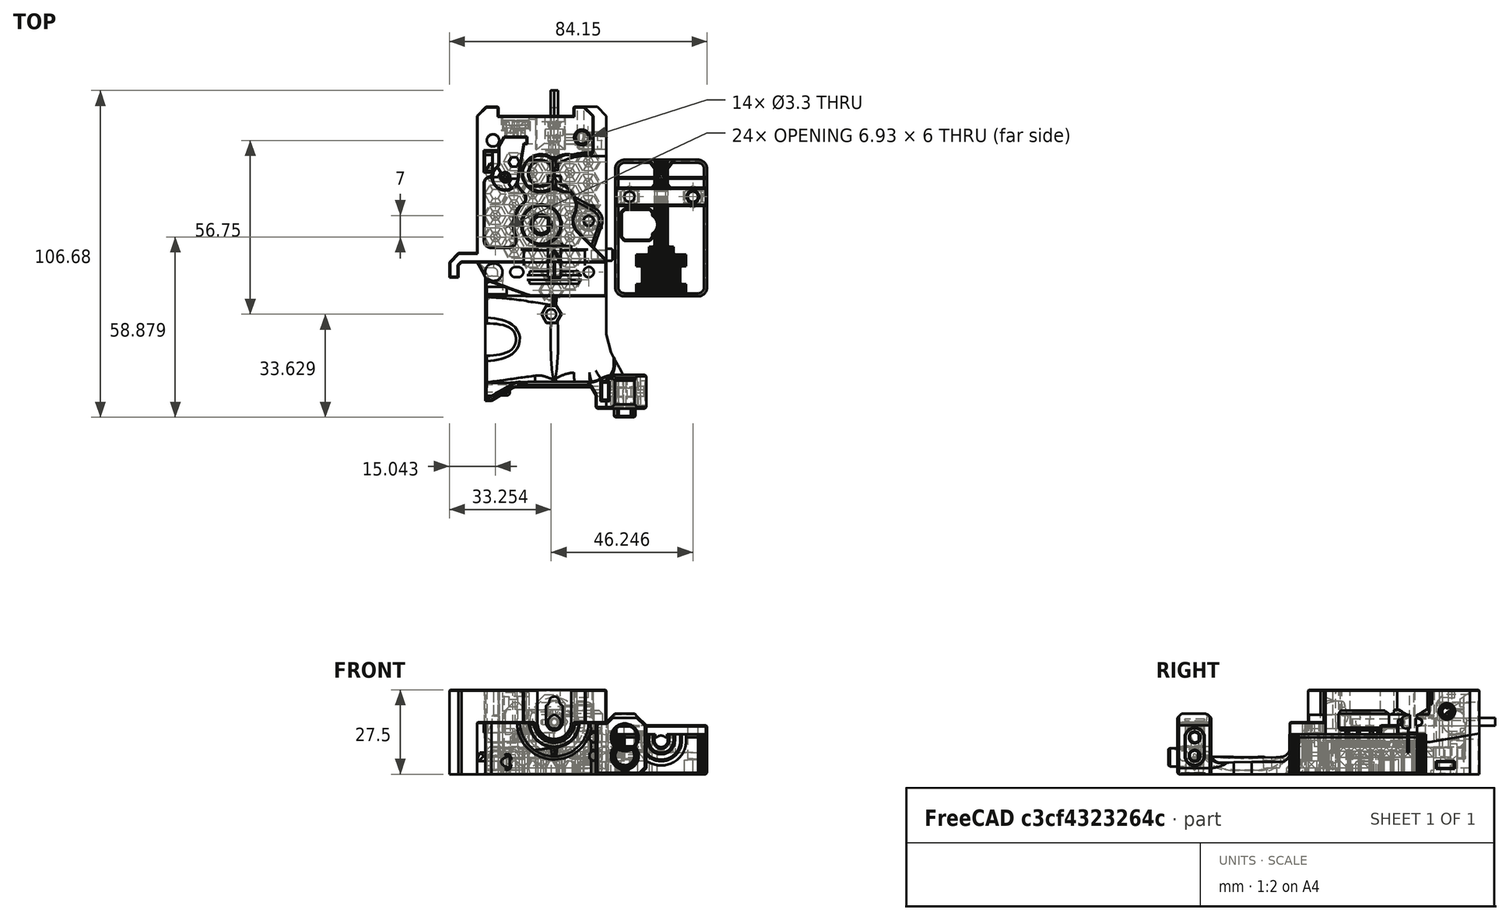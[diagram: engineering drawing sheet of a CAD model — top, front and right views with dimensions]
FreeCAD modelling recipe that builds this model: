
FCSTD DOCUMENT  (FreeCAD 0.18R14555 (Git shallow))
Label: PTFE-BMG-v2
License: All rights reserved
LicenseURL: http://en.wikipedia.org/wiki/All_rights_reserved
objects: Part::Cut×34, Part::Feature×32, Part::Box×29, Part::Cylinder×24, Part::MultiFuse×20, Part::Chamfer×8, Part::MultiCommon×4, App::DocumentObjectGroup×3, Sketcher::SketchObject×1, PartDesign::Pad×1, PartDesign::Body×1
note: 155 computed .brp shape members not serialized (recipe doc carries the construction recipe); baked Part::Feature solids carry a one-line shape summary decoded from their .brp

FEATURE [Part::Feature] Part__Feature001  label="ptfe-insert"
  Placement = pos=(4.72,10,0) rot=(0,0,1;0rad)
  shape: bbox 6.822 x 10.5 x 11.73 mm, 34 faces (baked)
FEATURE [Part::Feature] Part__Feature002  label="ptfe-path"
  Placement = pos=(4.72,17,0) rot=(0,0,1;0rad)
  shape: bbox 4.25 x 24 x 4.45 mm, 6 faces (baked)
FEATURE [Part::Feature] Part__Feature003  label="filament-path"
  Placement = pos=(4.72,30,0) rot=(0,0,1;0rad)
  shape: bbox 2.35 x 16 x 2.55 mm, 14 faces (baked)
FEATURE [Part::Feature] PTFE_CUTTER_1_0_1_001001_solid  label="PTFE_CUTTER"
  Placement = pos=(37.03,-6.87,0) rot=(0,0,1;0rad)
  shape: bbox 30 x 35 x 16 mm, 2095 faces (baked)
FEATURE [Part::Box] Box  label="Cube"
  AttacherType = Attacher::AttachEngine3D
  Height = 17
  Length = 33
  Placement = pos=(20,6,0) rot=(0,0,1;0rad)
  Width = 1
FEATURE [Part::Feature] PTFE_CUTTER_1_0_1_001001_solid001  label="PTFE_CUTTER001"
  Placement = pos=(37.03,-6.87,0) rot=(0,0,1;0rad)
  shape: bbox 30 x 35 x 16 mm, 2095 faces (baked)
FEATURE [Part::MultiCommon] Common
  Placement = pos=(0,18.58,0) rot=(0,0,1;0rad)
  Shapes = -> [Box,PTFE_CUTTER_1_0_1_001001_solid001]
FEATURE [Part::Box] Box001  label="Cube001"
  AttacherType = Attacher::AttachEngine3D
  Height = 18
  Length = 32
  Placement = pos=(20,16.32,0) rot=(0,0,1;0rad)
  Width = 6
FEATURE [Part::Box] Box002  label="Cube002"
  AttacherType = Attacher::AttachEngine3D
  Height = 18
  Length = 32
  Placement = pos=(20,16,0) rot=(0,0,1;0rad)
  Width = 15
FEATURE [Part::Feature] PTFE_CUTTER_1_0_1_001001_solid002  label="PTFE_CUTTER002"
  Placement = pos=(37.03,-6.87,0) rot=(0,0,1;0rad)
  shape: bbox 30 x 35 x 16 mm, 2095 faces (baked)
FEATURE [Part::MultiCommon] Common001
  Placement = pos=(0,9.58,0) rot=(0,0,1;0rad)
  Shapes = -> [Box002,PTFE_CUTTER_1_0_1_001001_solid002]
FEATURE [Part::Box] Box003  label="Cube003"
  AttacherType = Attacher::AttachEngine3D
  Height = 18
  Length = 32
  Placement = pos=(20,7,0) rot=(0,0,1;0rad)
  Width = 11
FEATURE [Part::Feature] PTFE_CUTTER_1_0_1_001001_solid003  label="PTFE_CUTTER003"
  Placement = pos=(37.03,-6.87,0) rot=(0,0,1;0rad)
  shape: bbox 30 x 35 x 16 mm, 2095 faces (baked)
FEATURE [Part::MultiCommon] Common002
  Placement = pos=(0,6.58,0) rot=(0,0,1;0rad)
  Shapes = -> [Box003,PTFE_CUTTER_1_0_1_001001_solid003]
FEATURE [Part::Cut] Cut
  Base = -> PTFE_CUTTER_1_0_1_001001_solid
  Tool = -> Box001
FEATURE [Part::MultiFuse] Fusion
  Shapes = -> [Cut,Common002,Common001,Common]
FEATURE [Part::Box] Box004  label="Cube004"
  AttacherType = Attacher::AttachEngine3D
  Height = 10
  Length = 10
  Placement = pos=(23,7,6) rot=(0,0,1;0rad)
  Width = 17.7
FEATURE [Part::Box] Box005  label="Cube005"
  AttacherType = Attacher::AttachEngine3D
  Height = 10
  Length = 10
  Placement = pos=(23,25.5,6) rot=(0,0,1;0rad)
  Width = 3.7
FEATURE [Part::MultiFuse] Fusion001
  Shapes = -> [Box005,Box004,Fusion]
FEATURE [Part::Box] Box006  label="Cube006"
  AttacherType = Attacher::AttachEngine3D
  Height = 5
  Length = 1
  Placement = pos=(49.88,-10,1) rot=(0,0,1;0rad)
  Width = 37.5
FEATURE [Part::MultiFuse] Fusion002
  Shapes = -> [Box006,Fusion001]
FEATURE [Part::Box] Box007  label="Cube007"
  AttacherType = Attacher::AttachEngine3D
  Height = 21
  Length = 32
  Placement = pos=(20,13,0) rot=(0,0,1;0rad)
  Width = 2
FEATURE [Part::Feature] Fusion002001  label="Fusion003"
  shape: bbox 30 x 44.58 x 16 mm, 1730 faces (baked)
FEATURE [Part::MultiCommon] Common003
  Placement = pos=(0,-7,0) rot=(0,0,1;0rad)
  Shapes = -> [Box007,Fusion002001]
FEATURE [Part::MultiFuse] Fusion002002
  Shapes = -> [Common003,Fusion002]
FEATURE [Part::Cylinder] Cylinder005  label="ptfe-cut002"
  Angle = 360
  AttacherType = Attacher::AttachEngine3D
  Height = 22
  Placement = pos=(31.19,9.89,0) rot=(0,0,1;0rad)
  Radius = 3.4
FEATURE [Part::Box] Box010  label="Cube010"
  AttacherType = Attacher::AttachEngine3D
  Height = 10
  Length = 32
  Placement = pos=(20,-15,13) rot=(0,0,1;0rad)
  Width = 47
FEATURE [Part::Box] Box011  label="Cube011"
  AttacherType = Attacher::AttachEngine3D
  Height = 24
  Length = 10
  Placement = pos=(23,5,0) rot=(0,0,1;0rad)
  Width = 9.77
FEATURE [Part::Chamfer] Chamfer
  Base = -> Box011
  Edges = 4 edges r=1: [Edge1,Edge3,Edge5,Edge7]
FEATURE [Part::Cylinder] Cylinder006  label="Cylinder"
  Angle = 360
  AttacherType = Attacher::AttachEngine3D
  Height = 30
  Placement = pos=(25.52,19,0) rot=(0,0,1;0rad)
  Radius = 1.65
FEATURE [Part::Cylinder] Cylinder007  label="Cylinder001"
  Angle = 360
  AttacherType = Attacher::AttachEngine3D
  Height = 30
  Placement = pos=(46.23,19,0) rot=(0,0,1;0rad)
  Radius = 1.65
FEATURE [Part::Box] Box012  label="Cube012"
  AttacherType = Attacher::AttachEngine3D
  Height = 3
  Length = 30
  Placement = pos=(20.88,17,13) rot=(0,0,1;0rad)
  Width = 6
FEATURE [Part::Box] Box013  label="Cube013"
  AttacherType = Attacher::AttachEngine3D
  Height = 4
  Length = 3.8
  Placement = pos=(33.98,16,12) rot=(0,0,1;0rad)
  Width = 8
FEATURE [Part::Cylinder] Cylinder008  label="ptfe-tube-pref002"
  Angle = 360
  AttacherType = Attacher::AttachEngine3D
  Height = 32
  Placement = pos=(35.85,27,10.6) rot=(1,0,0;1.5708rad)
  Radius = 2
FEATURE [Part::Cut] Cut001008
  Base = -> Box013
  Placement = pos=(0,1,0) rot=(0,0,1;0rad)
  Tool = -> Cylinder008
FEATURE [Part::Cylinder] Cylinder009  label="Cylinder002"
  Angle = 360
  AttacherType = Attacher::AttachEngine3D
  Height = 30
  Placement = pos=(25.52,20,0) rot=(0,0,1;0rad)
  Radius = 1.65
FEATURE [Part::Cylinder] Cylinder010  label="Cylinder003"
  Angle = 360
  AttacherType = Attacher::AttachEngine3D
  Height = 30
  Placement = pos=(46.23,20,0) rot=(0,0,1;0rad)
  Radius = 1.65
FEATURE [Part::MultiFuse] Fusion002005
  Shapes = -> [Cylinder009,Cylinder010]
FEATURE [Part::Feature] Cut001012003001  label="Cut001012004"
  Placement = pos=(25.52,19,0) rot=(0,0,1;0rad)
  shape: bbox 5.543 x 6.4 x 5 mm, 28 faces (baked)
FEATURE [Part::Feature] Cut001012003002  label="Cut001012005"
  Placement = pos=(46.23,19,0) rot=(0,0,1;0rad)
  shape: bbox 5.543 x 6.4 x 5 mm, 28 faces (baked)
FEATURE [Part::Feature] Body001005  label="Body001"
  Placement = pos=(35.88,25.2,0) rot=(0,0,1;0rad)
  shape: bbox 6.881 x 4.788 x 40 mm, 8 faces (baked)
FEATURE [Part::Feature] Body001006  label="Body002"
  Placement = pos=(35.88,26.02,0) rot=(0,0,1;3.14159rad)
  shape: bbox 12.97 x 8.755 x 40 mm, 8 faces (baked)
FEATURE [Part::Feature] Body001007  label="Body003"
  Placement = pos=(35.88,25.2,10.5) rot=(0,0,1;0rad)
  shape: bbox 12.18 x 7.934 x 34 mm, 5 faces (baked)
FEATURE [Part::MultiFuse] Fusion002008
  Placement = pos=(0,0,7) rot=(0,0,1;0rad)
  Shapes = -> [Body001005,Body001006]
FEATURE [Part::Cut] Cut001012003003
  Base = -> Fusion002002
  Tool = -> Fusion002008
FEATURE [Part::Cut] Cut001012003004
  Base = -> Cut001012003003
  Tool = -> Body001007
FEATURE [Part::Cut] Cut001012003005
  Base = -> Cut001012003004
  Tool = -> Cylinder005
FEATURE [Part::Cut] Cut001012003006
  Base = -> Cut001012003005
  Tool = -> Chamfer
FEATURE [Part::Feature] Part__Feature008  label="filament-path001"
  Placement = pos=(4.72,40,0) rot=(0,0,1;0rad)
  shape: bbox 2.35 x 16 x 2.55 mm, 14 faces (baked)
FEATURE [Part::Cut] Cut001012003011002008002
  Base = -> Cut001012003006
  Tool = -> Cylinder006
FEATURE [Part::Cut] Cut001012003011002008003
  Base = -> Cut001012003011002008002
  Tool = -> Cylinder007
FEATURE [Part::Cut] Cut001012003011002008004
  Base = -> Cut001012003011002008003
  Tool = -> Cut001012003002
FEATURE [Part::Cut] Cut001012003011002008005
  Base = -> Cut001012003011002008004
  Tool = -> Cut001012003001
FEATURE [Part::Cut] Cut001012003011002008006  label="cutter-base"
  Base = -> Cut001012003011002008005
  Tool = -> Box010
FEATURE [Part::Feature] Cut001012003011002008006002  label="cutter-base001"
  shape: bbox 30 x 44.58 x 13 mm, 1519 faces (baked)
FEATURE [Part::Chamfer] Chamfer002002
  Base = -> Cut001012003011002008006002
  Edges = 37 edges r=0.4: [Edge442,Edge443,Edge444,Edge445,Edge446,Edge447,Edge448,Edge449,Edge450,Edge451,Edge452,Edge453,Edge454,Edge455,Edge456,Edge457,Edge458,Edge459,Edge460,Edge461,Edge462,Edge463,Edge464,Edge465,Edge546,Edge549,Edge550,Edge551,Edge552,Edge553,Edge592,Edge593,Edge594,Edge595,Edge596,Edge597,Edge1307]
FEATURE [Part::Chamfer] Chamfer002003  label="cutter-base-rf"
  Base = -> Chamfer002002
  Edges = 8 edges r=1: [Edge389,Edge392,Edge417,Edge421,Edge506,Edge508,Edge530,Edge534]
FEATURE [Part::Box] Box019  label="Cube019"
  AttacherType = Attacher::AttachEngine3D
  Height = 10
  Length = 10
  Placement = pos=(30,23,8) rot=(0,0,1;0rad)
  Width = 10
FEATURE [Part::Cut] Cut001012003011002008006003
  Base = -> Cut001008
  Tool = -> Box019
FEATURE [Part::Cut] Cut001012003011002008006004
  Base = -> Box012
  Tool = -> Fusion002005
FEATURE [Part::MultiFuse] Fusion002009
  Shapes = -> [Cut001012003011002008006004,Cut001012003011002008006003]
FEATURE [Part::Chamfer] Chamfer002004  label="cutter-cap"
  Base = -> Fusion002009
  Edges = 13 edges r=0.4: [Edge1,Edge2,Edge3,Edge7,Edge8,Edge17,Edge18,Edge31,Edge32,Edge33,Edge34,Edge35,Edge41]
  Placement = pos=(0,-1,0) rot=(0,0,1;0rad)
FEATURE [Part::Box] Box028  label="Cube028"
  AttacherType = Attacher::AttachEngine3D
  Height = 3.35
  Length = 8
  Placement = pos=(8.5,8.5,10.7) rot=(0,0,1;0rad)
  Width = 1
FEATURE [Part::Box] Box029  label="hingle-support-p3"
  AttacherType = Attacher::AttachEngine3D
  Height = 3.35
  Length = 7
  Placement = pos=(8.5,12.8,10.7) rot=(0,0,1;0rad)
  Width = 1
FEATURE [Part::Box] Box030  label="hingle-support-p4"
  AttacherType = Attacher::AttachEngine3D
  Height = 3.35
  Length = 5
  Placement = pos=(9,15.1,10.7) rot=(0,0,1;0rad)
  Width = 1
FEATURE [Part::Box] Box031  label="Cube031"
  AttacherType = Attacher::AttachEngine3D
  Height = 3.35
  Length = 3
  Placement = pos=(11.7,4.8,10.7) rot=(0,0,1;0rad)
  Width = 1
FEATURE [Part::Chamfer] Chamfer002005  label="hingle-support-p2"
  Base = -> Box028
  Edges = 1 edges r=0.5: [Edge1]
FEATURE [Part::Chamfer] Chamfer002006  label="hingle-support-p1"
  Base = -> Box031
  Edges = 1 edges r=0.5: [Edge1]
FEATURE [Part::Cylinder] Cylinder015  label="Cylinder008"
  Angle = 360
  AttacherType = Attacher::AttachEngine3D
  Height = 10
  Placement = pos=(24,-43,6) rot=(1,0,0;1.5708rad)
  Radius = 3.5
FEATURE [Part::Cylinder] Cylinder016  label="Cylinder009"
  Angle = 360
  AttacherType = Attacher::AttachEngine3D
  Height = 10
  Placement = pos=(24,-43,11.5) rot=(1,0,0;1.5708rad)
  Radius = 3.6
FEATURE [Part::Cut] Cut001012003011002008006006009003002
  Base = -> Cylinder015
  Tool = -> Cylinder016
FEATURE [Part::Cylinder] Cylinder017  label="Cylinder010"
  Angle = 360
  AttacherType = Attacher::AttachEngine3D
  Height = 10
  Placement = pos=(19,-48,6) rot=(0,1,0;1.5708rad)
  Radius = 1.65
FEATURE [Part::Cylinder] Cylinder018  label="Cylinder011"
  Angle = 360
  AttacherType = Attacher::AttachEngine3D
  Height = 10
  Placement = pos=(19,-46.6,6) rot=(0,1,0;1.5708rad)
  Radius = 0.5
FEATURE [Part::Cut] Cut001012003011002008006006009003003
  Base = -> Cut001012003011002008006006009003002
  Tool = -> Cylinder017
FEATURE [Part::Cut] Cut001012003011002008006006009003004
  Base = -> Cut001012003011002008006006009003003
  Tool = -> Cylinder018
FEATURE [Part::Chamfer] Chamfer002007  label="brope-spacer"
  Base = -> Cut001012003011002008006006009003004
  Edges = 8 edges r=0.4: [Edge1,Edge2,Edge8,Edge12,Edge13,Edge14,Edge15,Edge16]
FEATURE [Part::Box] Box034  label="probe-support002"
  AttacherType = Attacher::AttachEngine3D
  Height = 0.2
  Length = 9
  Placement = pos=(22,-49,0) rot=(0,0,1;0rad)
  Width = 8
FEATURE [Part::Box] Box035  label="probe-support-mid"
  AttacherType = Attacher::AttachEngine3D
  Height = 0.2
  Length = 9
  Placement = pos=(19.5,-49,8.9) rot=(0,0,1;0rad)
  Width = 8
FEATURE [App::DocumentObjectGroup] Group  label="Cutter-guide"
  Group = -> [Cut001012003011002008006,Chamfer002003,Chamfer002004]
FEATURE [App::DocumentObjectGroup] Group002  label="Other"
  Group = -> [Chamfer002007]
FEATURE [Part::Feature] Cut001012003011002008006006009003008001  label="hex-cut-origin-p003"
  shape: bbox 6.928 x 6 x 4 mm, 14 faces (baked)
FEATURE [Part::Feature] Cut001012003011002008006006009003007001  label="hex-cut-origin-p004"
  shape: bbox 37.24 x 34 x 4 mm, 336 faces, 24 solids (baked)
FEATURE [Part::Feature] Cut001012003011002008006006009003008002  label="hex-cut-origin-p005"
  Placement = pos=(0,0,2.5) rot=(0,0,1;0rad)
  shape: bbox 6.928 x 6 x 4 mm, 14 faces (baked)
FEATURE [Part::Feature] Cut001012003011002008006006009003008003  label="hex-cut-origin-p006"
  Placement = pos=(0,0,2.5) rot=(0,0,1;0rad)
  shape: bbox 37.24 x 34 x 4 mm, 336 faces, 24 solids (baked)
FEATURE [Part::Feature] Cut001012003011002008006006009003008004  label="hex-cut-origin-p007"
  Placement = pos=(0,0,5) rot=(0,0,1;0rad)
  shape: bbox 37.24 x 34 x 4 mm, 336 faces, 24 solids (baked)
FEATURE [Part::MultiFuse] Fusion002010004002002006  label="full-back-hex-cut"
  Shapes = -> [Cut001012003011002008006006009003008001,Cut001012003011002008006006009003008003,Cut001012003011002008006006009003007001,Cut001012003011002008006006009003008002,Cut001012003011002008006006009003008004]
FEATURE [Part::Cylinder] Cylinder  label="scew-hole"
  Angle = 360
  AttacherType = Attacher::AttachEngine3D
  Height = 11
  Placement = pos=(12.25,11.13,0) rot=(0,0,1;0rad)
  Radius = 1.6
FEATURE [Part::Cylinder] Cylinder020  label="Cylinder013"
  Angle = 360
  AttacherType = Attacher::AttachEngine3D
  Height = 3.4
  Radius = 3
FEATURE [Part::Box] Box038  label="Cube032"
  AttacherType = Attacher::AttachEngine3D
  Height = 0.2
  Length = 5
  Placement = pos=(1.6,-5,3.2) rot=(0,0,1;0rad)
  Width = 10
FEATURE [Part::Box] Box039  label="Cube033"
  AttacherType = Attacher::AttachEngine3D
  Height = 0.2
  Length = 5
  Placement = pos=(-6.6,-5,3.2) rot=(0,0,1;0rad)
  Width = 10
FEATURE [Part::Box] Box040  label="Cube034"
  AttacherType = Attacher::AttachEngine3D
  Height = 0.4
  Length = 10
  Placement = pos=(-5,-6.6,3) rot=(0,0,1;0rad)
  Width = 5
FEATURE [Part::Box] Box041  label="Cube035"
  AttacherType = Attacher::AttachEngine3D
  Height = 0.4
  Length = 10
  Placement = pos=(-5,1.6,3) rot=(0,0,1;0rad)
  Width = 5
FEATURE [Part::MultiFuse] Fusion002010004002002006003002002002
  Shapes = -> [Box039,Box041,Box038,Box040]
FEATURE [Part::Cut] Cut001012003011002008006006009003008009
  Base = -> Cylinder020
  Placement = pos=(12.25,11.13,0) rot=(0,0,1;0rad)
  Tool = -> Fusion002010004002002006003002002002
FEATURE [Part::Cylinder] Cylinder022  label="screw-base-fill"
  Angle = 360
  AttacherType = Attacher::AttachEngine3D
  Height = 7
  Placement = pos=(12.25,11.13,0) rot=(0,0,1;0rad)
  Radius = 5.3
FEATURE [Part::MultiFuse] Fusion002010004002002006003002002004  label="back-screw"
  Shapes = -> [Cut001012003011002008006006009003008009,Cylinder]
FEATURE [Part::Feature] Fusion002010004002002006003002002004001  label="back-screw001"
  shape: bbox 6 x 6 x 11 mm, 16 faces (baked)
FEATURE [Part::Box] Box043  label="Cube037"
  AttacherType = Attacher::AttachEngine3D
  Height = 11.5
  Length = 2.2
  Placement = pos=(0,38.98,0) rot=(0,0,1;0rad)
  Width = 9.15
FEATURE [Part::Feature] Part__Feature025009  label="Original-v2"
  Placement = pos=(-24,-68,-52.6717) rot=(0,0,1;0rad)
  shape: bbox 64.27 x 98.52 x 42.65 mm, 988 faces (baked)
FEATURE [Part::Feature] Part__Feature025009001  label="Original-v003"
  Placement = pos=(-24,-68,-52.6717) rot=(0,0,1;0rad)
  shape: bbox 64.27 x 98.52 x 42.65 mm, 988 faces (baked)
FEATURE [Part::MultiFuse] Fusion002010004002002006003002002004003  label="full-custom-support"
  Shapes = -> [Box034,Box035,Chamfer002006,Chamfer002005,Box029,Box030]
FEATURE [App::DocumentObjectGroup] Group001  label="Support"
  Group = -> [Fusion002010004002002006003002002004003]
FEATURE [Part::Feature] Fusion002010004002002006002001  label="full-filament-path001"
  shape: bbox 2.35 x 26 x 2.55 mm, 5 faces (baked)
FEATURE [Part::MultiFuse] Fusion002010004002002006002  label="full-filament-path"
  Shapes = -> [Part__Feature008,Part__Feature003]
FEATURE [Part::Feature] Part__Feature002001  label="ptfp1"
  Placement = pos=(4.72,17,0) rot=(0,0,1;0rad)
  shape: bbox 4.25 x 24 x 4.45 mm, 6 faces (baked)
FEATURE [Part::MultiFuse] Fusion002010004002002006003002002004003002  label="full-ptfe-path"
  Shapes = -> [Part__Feature002,Part__Feature001]
FEATURE [Part::Feature] Part__Feature025009002  label="ptfp002"
  Placement = pos=(4.72,8,0) rot=(0,0,1;0rad)
  shape: bbox 4.25 x 24 x 4.45 mm, 6 faces (baked)
FEATURE [Part::MultiFuse] Fusion002010004002002006003002002004003003  label="long-ptfe-path"
  Shapes = -> [Part__Feature025009002,Part__Feature002001]
FEATURE [Part::Feature] Fusion002010004002002006003002002004003003001  label="long-ptfe-path001"
  shape: bbox 4.25 x 33 x 4.45 mm, 6 faces (baked)
FEATURE [Part::Cut] Cut001012003011002008006006009003008010
  Base = -> Part__Feature025009001
  Tool = -> Fusion002010004002002006003002002004003003001
FEATURE [Part::Cut] Cut001012003011002008006006009003008011
  Base = -> Cut001012003011002008006006009003008010
  Tool = -> Fusion002010004002002006002001
FEATURE [Part::Cylinder] Cylinder023  label="bolt-fill"
  Angle = 360
  AttacherType = Attacher::AttachEngine3D
  Height = 10
  Placement = pos=(1,33.38,7) rot=(-1,0,0;1.5708rad)
  Radius = 3
FEATURE [Part::Cylinder] Cylinder024  label="top-m3"
  Angle = 360
  AttacherType = Attacher::AttachEngine3D
  Height = 10
  Placement = pos=(1,33.38,7) rot=(-1,0,0;1.5708rad)
  Radius = 1.65
FEATURE [Part::Cylinder] Cylinder025  label="m3-printable-cut"
  Angle = 360
  AttacherType = Attacher::AttachEngine3D
  Height = 10
  Placement = pos=(1,33.38,8.5) rot=(-1,0,0;1.5708rad)
  Radius = 0.5
FEATURE [Part::Box] Box044  label="m3-square-nut"
  AttacherType = Attacher::AttachEngine3D
  Height = 10
  Length = 5.8
  Placement = pos=(-1.9,39,0) rot=(0,0,1;0rad)
  Width = 2.2
FEATURE [Part::Cylinder] Cylinder026  label="Cylinder014"
  Angle = 360
  AttacherType = Attacher::AttachEngine3D
  Height = 9.2
  Placement = pos=(4.53,37.9,20.5) rot=(0,1,0;1.5708rad)
  Radius = 3
FEATURE [Part::Cylinder] Cylinder027  label="m3"
  Angle = 360
  AttacherType = Attacher::AttachEngine3D
  Height = 9.2
  Placement = pos=(4.53,37.9,20.5) rot=(0,1,0;1.5708rad)
  Radius = 1.65
FEATURE [Part::Cylinder] Cylinder028  label="m004"
  Angle = 360
  AttacherType = Attacher::AttachEngine3D
  Height = 9.2
  Placement = pos=(4.53,37.9,22) rot=(0,1,0;1.5708rad)
  Radius = 0.5
FEATURE [Part::Box] Box045  label="Cube038"
  AttacherType = Attacher::AttachEngine3D
  Height = 6
  Length = 2.2
  Placement = pos=(8.53,34.9,17.6) rot=(0,0,1;0rad)
  Width = 19
FEATURE [Part::Cylinder] Cylinder029  label="Cylinder015"
  Angle = 360
  AttacherType = Attacher::AttachEngine3D
  Height = 14
  Placement = pos=(24,-51,15.8) rot=(-1,0,0;1.5708rad)
  Radius = 0.7
FEATURE [Part::Cylinder] Cylinder030  label="Cylinder016"
  Angle = 360
  AttacherType = Attacher::AttachEngine3D
  Height = 23
  Placement = pos=(35,-44.5,7.5) rot=(0,-1,0;1.5708rad)
  Radius = 0.5
FEATURE [Part::Cylinder] Cylinder031  label="Cylinder017"
  Angle = 360
  AttacherType = Attacher::AttachEngine3D
  Height = 23
  Placement = pos=(35,-44.5,13.5) rot=(0,-1,0;1.5708rad)
  Radius = 0.5
FEATURE [Part::Box] Box046  label="Cube039"
  AttacherType = Attacher::AttachEngine3D
  Height = 12.9
  Length = 2.2
  Placement = pos=(16.46,-47.37,9.1) rot=(0,0,1;0rad)
  Width = 5.8
FEATURE [Part::Box] Box047  label="Cube040"
  AttacherType = Attacher::AttachEngine3D
  Height = 2.2
  Length = 10
  Placement = pos=(8.98,34.48,1.8) rot=(0,0,1;0rad)
  Width = 5.8
FEATURE [Part::Cylinder] Cylinder032  label="Cylinder018"
  Angle = 360
  AttacherType = Attacher::AttachEngine3D
  Height = 10
  Placement = pos=(-11.57,36,12.66) rot=(-1,0,0;1.5708rad)
  Radius = 0.5
FEATURE [Part::Cylinder] Cylinder033  label="Cylinder019"
  Angle = 360
  AttacherType = Attacher::AttachEngine3D
  Height = 10
  Placement = pos=(-11.57,40.88,12.96) rot=(-1,0,0;1.5708rad)
  Radius = 0.5
FEATURE [Part::Feature] Fusion002010004002002006003002002004003003005  label="full-custom-support003"
  shape: bbox 22.5 x 65.1 x 14.05 mm, 38 faces, 6 solids (baked)
FEATURE [Part::Feature] Fusion002010004002002006003002002004003003006  label="back-screw002"
  Placement = pos=(0,0,1) rot=(0,0,1;0rad)
  shape: bbox 6 x 6 x 11 mm, 16 faces (baked)
FEATURE [Part::MultiFuse] Fusion002010004002002006003002002004003003007  label="hingle-screw"
  Shapes = -> [Fusion002010004002002006003002002004003003006,Fusion002010004002002006003002002004001]
FEATURE [Part::Feature] Fusion002010004002002006003002002004003003007001  label="hingle-screw001"
  shape: bbox 6 x 6 x 12 mm, 16 faces (baked)
FEATURE [Part::MultiFuse] Fusion002010004002002006003002002004003003007002
  Shapes = -> [Cylinder022,Cut001012003011002008006006009003008011]
FEATURE [Part::Cut] Cut001012003011002008006006009003008012
  Base = -> Fusion002010004002002006003002002004003003007002
  Tool = -> Fusion002010004002002006003002002004003003007001
FEATURE [Part::Cut] Cut001012003011002008006006009003008013
  Base = -> Cut001012003011002008006006009003008012
  Tool = -> Box047
FEATURE [Part::MultiFuse] Fusion002010004002002006003002002004003003007003
  Shapes = -> [Cylinder023,Cut001012003011002008006006009003008013]
FEATURE [Part::Cut] Cut001012003011002008006006009003008014
  Base = -> Fusion002010004002002006003002002004003003007003
  Tool = -> Cylinder024
FEATURE [Part::Cut] Cut001012003011002008006006009003008015
  Base = -> Cut001012003011002008006006009003008014
  Tool = -> Cylinder025
FEATURE [Part::Cut] Cut001012003011002008006006009003008016
  Base = -> Cut001012003011002008006006009003008015
  Tool = -> Box044
FEATURE [Part::MultiFuse] Fusion002010004002002006003002002004003003007004
  Shapes = -> [Cut001012003011002008006006009003008016,Cylinder026]
FEATURE [Part::Cut] Cut001012003011002008006006009003008017
  Base = -> Fusion002010004002002006003002002004003003007004
  Tool = -> Cylinder027
FEATURE [Part::Cut] Cut001012003011002008006006009003008018
  Base = -> Cut001012003011002008006006009003008017
  Tool = -> Cylinder028
FEATURE [Part::Cut] Cut001012003011002008006006009003008019
  Base = -> Cut001012003011002008006006009003008018
  Tool = -> Box045
FEATURE [Part::Cut] Cut001012003011002008006006009003008020
  Base = -> Cut001012003011002008006006009003008019
  Tool = -> Cylinder032
FEATURE [Part::Cut] Cut001012003011002008006006009003008021
  Base = -> Cut001012003011002008006006009003008020
  Tool = -> Cylinder033
FEATURE [Part::Cut] Cut001012003011002008006006009003008022
  Base = -> Cut001012003011002008006006009003008021
  Tool = -> Cylinder031
FEATURE [Part::Cut] Cut001012003011002008006006009003008023
  Base = -> Cut001012003011002008006006009003008022
  Tool = -> Cylinder030
FEATURE [Part::Cut] Cut001012003011002008006006009003008024
  Base = -> Cut001012003011002008006006009003008023
  Tool = -> Cylinder029
FEATURE [Part::Box] Box048  label="Cube041"
  AttacherType = Attacher::AttachEngine3D
  Height = 8.9
  Length = 2.2
  Placement = pos=(16.46,-47.37,-4e-16) rot=(0,0,1;0rad)
  Width = 5.8
FEATURE [Part::Cut] Cut001012003011002008006006009003008025
  Base = -> Cut001012003011002008006006009003008024
  Tool = -> Box046
FEATURE [Part::Cut] Cut001012003011002008006006009003008026
  Base = -> Cut001012003011002008006006009003008025
  Tool = -> Box048
FEATURE [Part::Chamfer] Chamfer002008  label="rev1-draf"
  Base = -> Cut001012003011002008006006009003008026
  Edges = 12 edges r=0.4: [Edge292,Edge509,Edge511,Edge719,Edge725,Edge726,Edge1061,Edge1063,Edge1529,Edge1541,Edge2207,Edge2212]
FEATURE [Part::Feature] Chamfer002008001  label="rev1-refined"
  shape: bbox 64.27 x 98.52 x 42.65 mm, 1032 faces (baked)
FEATURE [Sketcher::SketchObject] Sketch
  MapMode = 5
  Support = -> [XY_Plane]
  sketch-geometry (47):
    g0: LineSegment StartX=2 StartY=-15 StartZ=0 EndX=-2 EndY=-15 EndZ=0
    g1: LineSegment StartX=-2 StartY=-15 StartZ=0 EndX=-4 EndY=-11.5 EndZ=0
    g2: LineSegment StartX=-4 StartY=-11.5 StartZ=0 EndX=-2 EndY=-8 EndZ=0
    g3: LineSegment StartX=-2 StartY=-8 StartZ=0 EndX=-4 EndY=-4.5 EndZ=0
    g4: LineSegment StartX=-4 StartY=-4.5 StartZ=0 EndX=-8 EndY=-4.5 EndZ=0
    g5: LineSegment StartX=-8 StartY=-4.5 StartZ=0 EndX=-10 EndY=-1 EndZ=0
    g6: LineSegment StartX=-10 StartY=-1 StartZ=0 EndX=-14 EndY=-1 EndZ=0
    g7: LineSegment StartX=-14 StartY=-1 StartZ=0 EndX=-16 EndY=2.5 EndZ=0
    g8: LineSegment StartX=-16 StartY=2.5 StartZ=0 EndX=-20 EndY=2.5 EndZ=0
    g9: LineSegment StartX=-20 StartY=2.5 StartZ=0 EndX=-22 EndY=6 EndZ=0
    g10: LineSegment StartX=-22 StartY=6 StartZ=0 EndX=-20 EndY=9.5 EndZ=0
    g11: LineSegment StartX=-20 StartY=9.5 StartZ=0 EndX=-22 EndY=13 EndZ=0
    g12: LineSegment StartX=-22 StartY=13 StartZ=0 EndX=-20 EndY=16.5 EndZ=0
    g13: LineSegment StartX=-20 StartY=16.5 StartZ=0 EndX=-16 EndY=16.5 EndZ=0
    g14: LineSegment StartX=-16 StartY=16.5 StartZ=0 EndX=-14 EndY=20 EndZ=0
    g15: LineSegment StartX=-14 StartY=20 StartZ=0 EndX=-10 EndY=20 EndZ=0
    g16: LineSegment StartX=-10 StartY=20 StartZ=0 EndX=-8 EndY=23.5 EndZ=0
    g17: LineSegment StartX=-8 StartY=23.5 StartZ=0 EndX=-10 EndY=27 EndZ=0
    g18: LineSegment StartX=-10 StartY=27 StartZ=0 EndX=-8 EndY=30.5 EndZ=0
    g19: LineSegment StartX=-8 StartY=30.5 StartZ=0 EndX=-4 EndY=30.5 EndZ=0
    g20: LineSegment StartX=-4 StartY=30.5 StartZ=0 EndX=-2 EndY=34 EndZ=0
    g21: LineSegment StartX=-2 StartY=34 StartZ=0 EndX=2 EndY=34 EndZ=0
    g22: LineSegment StartX=2 StartY=34 StartZ=0 EndX=4 EndY=30.5 EndZ=0
    g23: LineSegment StartX=4 StartY=30.5 StartZ=0 EndX=8 EndY=30.5 EndZ=0
    g24: LineSegment StartX=8 StartY=30.5 StartZ=0 EndX=10 EndY=34 EndZ=0
    g25: LineSegment StartX=10 StartY=34 StartZ=0 EndX=14 EndY=34 EndZ=0
    g26: LineSegment StartX=14 StartY=34 StartZ=0 EndX=16 EndY=30.5 EndZ=0
    g27: LineSegment StartX=16 StartY=30.5 StartZ=0 EndX=14 EndY=27 EndZ=0
    g28: LineSegment StartX=14 StartY=27 StartZ=0 EndX=16 EndY=23.5 EndZ=0
    g29: LineSegment StartX=16 StartY=23.5 StartZ=0 EndX=14 EndY=20 EndZ=0
    g30: LineSegment StartX=14 StartY=20 StartZ=0 EndX=16 EndY=16.5 EndZ=0
    g31: LineSegment StartX=16 StartY=16.5 StartZ=0 EndX=15 EndY=15 EndZ=0
    g32: LineSegment StartX=15 StartY=15 StartZ=0 EndX=14.5 EndY=15.5 EndZ=0
    g33: LineSegment StartX=14.5 StartY=15.5 StartZ=0 EndX=14 EndY=16 EndZ=0
    g34: LineSegment StartX=14 StartY=16 StartZ=0 EndX=11 EndY=16 EndZ=0
    g35: LineSegment StartX=11 StartY=16 StartZ=0 EndX=9 EndY=14.5 EndZ=0
    g36: LineSegment StartX=9 StartY=14.5 StartZ=0 EndX=8 EndY=12 EndZ=0
    g37: LineSegment StartX=8 StartY=12 StartZ=0 EndX=8 EndY=9.5 EndZ=0
    g38: LineSegment StartX=8 StartY=9.5 StartZ=0 EndX=9.5 EndY=7 EndZ=0
    g39: LineSegment StartX=9.5 StartY=7 StartZ=0 EndX=10 EndY=6 EndZ=0
    g40: LineSegment StartX=10 StartY=6 StartZ=0 EndX=8 EndY=2.5 EndZ=0
    g41: LineSegment StartX=8 StartY=2.5 StartZ=0 EndX=10 EndY=-1 EndZ=0
    g42: LineSegment StartX=10 StartY=-1 StartZ=0 EndX=8 EndY=-4.5 EndZ=0
    g43: LineSegment StartX=8 StartY=-4.5 StartZ=0 EndX=10 EndY=-8 EndZ=0
    g44: LineSegment StartX=10 StartY=-8 StartZ=0 EndX=8 EndY=-11.5 EndZ=0
    g45: LineSegment StartX=8 StartY=-11.5 StartZ=0 EndX=4 EndY=-11.5 EndZ=0
    g46: LineSegment StartX=4 StartY=-11.5 StartZ=0 EndX=2 EndY=-15 EndZ=0
  constraints (45):
    c: Coincident(g0,g1)
    c: Coincident(g1,g2)
    c: Coincident(g2,g3)
    c: Coincident(g3,g4)
    c: Coincident(g4,g5)
    c: Coincident(g5,g6)
    c: Coincident(g6,g7)
    c: Coincident(g7,g8)
    c: Coincident(g8,g9)
    c: Coincident(g9,g10)
    c: Coincident(g10,g11)
    c: Coincident(g11,g12)
    c: Coincident(g12,g13)
    c: Coincident(g13,g14)
    c: Coincident(g14,g15)
    c: Coincident(g15,g16)
    c: Coincident(g17,g18)
    c: Coincident(g18,g19)
    c: Coincident(g19,g20)
    c: Coincident(g20,g21)
    c: Coincident(g21,g22)
    c: Coincident(g22,g23)
    c: Coincident(g23,g24)
    c: Coincident(g24,g25)
    c: Coincident(g25,g26)
    c: Coincident(g26,g27)
    c: Coincident(g27,g28)
    c: Coincident(g28,g29)
    c: Coincident(g29,g30)
    c: Coincident(g30,g31)
    c: Coincident(g31,g32)
    c: Coincident(g32,g33)
    c: Coincident(g33,g34)
    c: Coincident(g34,g35)
    c: Coincident(g35,g36)
    c: Coincident(g36,g37)
    c: Coincident(g37,g38)
    c: Coincident(g38,g39)
    c: Coincident(g39,g40)
    c: Coincident(g40,g41)
    c: Coincident(g41,g42)
    c: Coincident(g42,g43)
    c: Coincident(g43,g44)
    c: Coincident(g44,g45)
    c: Coincident(g45,g46)
FEATURE [PartDesign::Pad] Pad
  Length = 0.2
  Length2 = 100
  Profile = -> Sketch
  Type = 0
FEATURE [PartDesign::Body] Body  label="hex-support"
  Group = -> [Sketch,Pad]
  Origin = -> Origin
  Tip = -> Pad
FEATURE [Part::Feature] Body001008  label="hex-support001"
  shape: bbox 38 x 49 x 0.2 mm, 49 faces (baked)
FEATURE [Part::MultiFuse] Fusion002010004002002006003002002004003003007005
  Shapes = -> [Fusion002010004002002006003002002004003003005,Body001008]
FEATURE [Part::MultiFuse] Fusion002010004002002006003002002004003003007006
  Shapes = -> [Fusion002010004002002006003002002004003003007005,Chamfer002008001]
